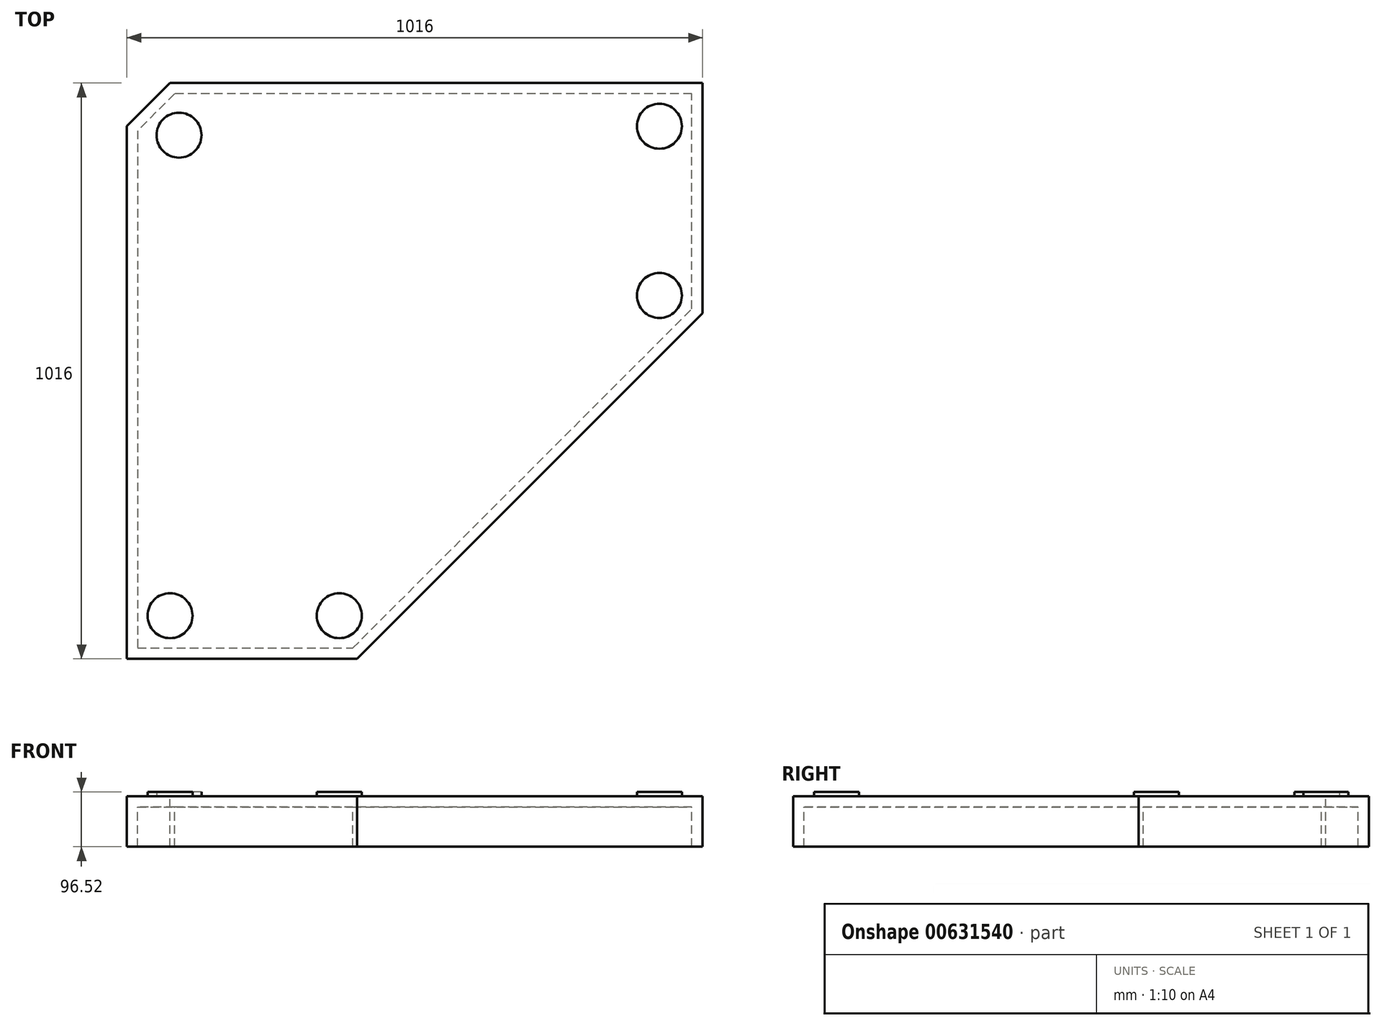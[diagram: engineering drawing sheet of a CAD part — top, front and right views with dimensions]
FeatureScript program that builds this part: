
annotation { "Feature Type Name" : "Feature", "Feature Type Description" : "" }
export const myFeature = defineFeature(function(context is Context, id is Id, definition is map)
    precondition{}
    {
        {
            var Q0;
            Q0=qCreatedBy(makeId("Top.planeOp"),FACE);
            var sketch = newSketch(context, id + "F0", { "sketchPlane" : qUnion([Q0])});
            skLineSegment(sketch, "E0", {"start": v(0, -1016) * mm, "end": v(406.4, -1016) * mm});
            skLineSegment(sketch, "E1", {"start": v(406.4, -1016) * mm, "end": v(1016, -406.4) * mm});
            skLineSegment(sketch, "E2", {"start": v(1016, -406.4) * mm, "end": v(1016, 0) * mm});
            skLineSegment(sketch, "E3", {"start": v(1016, 0) * mm, "end": v(76.2, 0) * mm});
            skLineSegment(sketch, "E4", {"start": v(76.2, 0) * mm, "end": v(0, -76.2) * mm});
            skLineSegment(sketch, "E5", {"start": v(0, -76.2) * mm, "end": v(0, -1016) * mm});
            skLineSegment(sketch, "E6.0", {"start": v(19.05, -996.95) * mm, "end": v(398.5, -996.95) * mm});
            skLineSegment(sketch, "E6.1", {"start": v(996.95, -398.5) * mm, "end": v(996.95, -19.05) * mm});
            skLineSegment(sketch, "E6.2", {"start": v(996.95, -19.05) * mm, "end": v(84.1, -19.05) * mm});
            skLineSegment(sketch, "E6.3", {"start": v(398.5, -996.95) * mm, "end": v(996.95, -398.5) * mm});
            skLineSegment(sketch, "E6.4", {"start": v(84.1, -19.05) * mm, "end": v(19.05, -84.1) * mm});
            skLineSegment(sketch, "E6.5", {"start": v(19.05, -84.1) * mm, "end": v(19.05, -996.95) * mm});
            skSolve(sketch);
        }
        {
            var Q0;
            Q0 = qSketchRegion(id + "F0", true);
            extrude(context, id + "F1", {"entities" : qUnion([Q0]), "oppositeDirection" : true, "depth" : 88.9 * mm, "offsetDistance" : 25.4 * mm});
        }
        {
            var Q0;
            Q0=makeQuery(id+"F0.imprint","IMPRINT",FACE,{"disambiguationData":[TD([[makeQuery(id+"F0.imprint","IMPRINT",EDGE,{"derivedFrom":sQuery(id+"F0.wireOp",EDGE,"E6.0")}),1.0]])]});
            extrude(context, id + "F2", {"entities" : qUnion([Q0]), "operationType" : NewBodyOperationType.ADD, "oppositeDirection" : true, "depth" : 19.05 * mm, "offsetDistance" : 25.4 * mm});
        }
        {
            var Q0;
            {var subQ0=sQuery(id+"F0.wireOp",EDGE,"E6.5");var subQ1=sQuery(id+"F0.wireOp",EDGE,"E6.4");var subQ2=sQuery(id+"F0.wireOp",EDGE,"E6.3");var subQ3=sQuery(id+"F0.wireOp",EDGE,"E6.2");var subQ4=sQuery(id+"F0.wireOp",EDGE,"E6.1");var subQ5=sQuery(id+"F0.wireOp",EDGE,"E6.0");Q0=makeQuery(id+"F2.boolean.opBoolean","MERGE",FACE,{"derivedFrom":[makeQuery(id+"F1.opExtrude","CAP_FACE",FACE,{"disambiguationData":[OSD([sQuery(id+"F0.wireOp",EDGE,"E0"),sQuery(id+"F0.wireOp",EDGE,"E1"),sQuery(id+"F0.wireOp",EDGE,"E2"),sQuery(id+"F0.wireOp",EDGE,"E3"),sQuery(id+"F0.wireOp",EDGE,"E4"),sQuery(id+"F0.wireOp",EDGE,"E5"),subQ5,subQ4,subQ3,subQ2,subQ1,subQ0])],"isStart":true}),makeQuery(id+"F2.opExtrude","CAP_FACE",FACE,{"disambiguationData":[OSD([subQ5,subQ4,subQ3,subQ2,subQ1,subQ0])],"isStart":true})]});}
            var sketch = newSketch(context, id + "F3", { "sketchPlane" : qUnion([Q0])});
            skLineSegment(sketch, "E7.0", {"start": v(939.8, -76.2) * mm, "end": v(107.76, -76.2) * mm, "construction": true});
            skLineSegment(sketch, "E7.1", {"start": v(76.2, -107.76) * mm, "end": v(76.2, -939.8) * mm, "construction": true});
            skLineSegment(sketch, "E7.2", {"start": v(76.2, -939.8) * mm, "end": v(374.84, -939.8) * mm, "construction": true});
            skLineSegment(sketch, "E7.3", {"start": v(107.76, -76.2) * mm, "end": v(76.2, -107.76) * mm, "construction": true});
            skLineSegment(sketch, "E7.4", {"start": v(374.84, -939.8) * mm, "end": v(939.8, -374.84) * mm, "construction": true});
            skLineSegment(sketch, "E7.5", {"start": v(939.8, -374.84) * mm, "end": v(939.8, -76.2) * mm, "construction": true});
            skCircle(sketch, "E8", {"center": v(76.2, -939.8) * mm, "radius": 39.69 * mm});
            skCircle(sketch, "E9", {"center": v(91.98, -91.98) * mm, "radius": 39.69 * mm});
            skCircle(sketch, "E10", {"center": v(374.84, -939.8) * mm, "radius": 39.69 * mm});
            skCircle(sketch, "E11", {"center": v(939.8, -374.84) * mm, "radius": 39.69 * mm});
            skCircle(sketch, "E12", {"center": v(939.8, -76.2) * mm, "radius": 39.69 * mm});
            skSolve(sketch);
        }
        {
            var Q0;
            Q0 = qSketchRegion(id + "F3", true);
            extrude(context, id + "F4", {"entities" : qUnion([Q0]), "operationType" : NewBodyOperationType.ADD, "depth" : 7.62 * mm, "offsetDistance" : 25.4 * mm});
        }
    });
